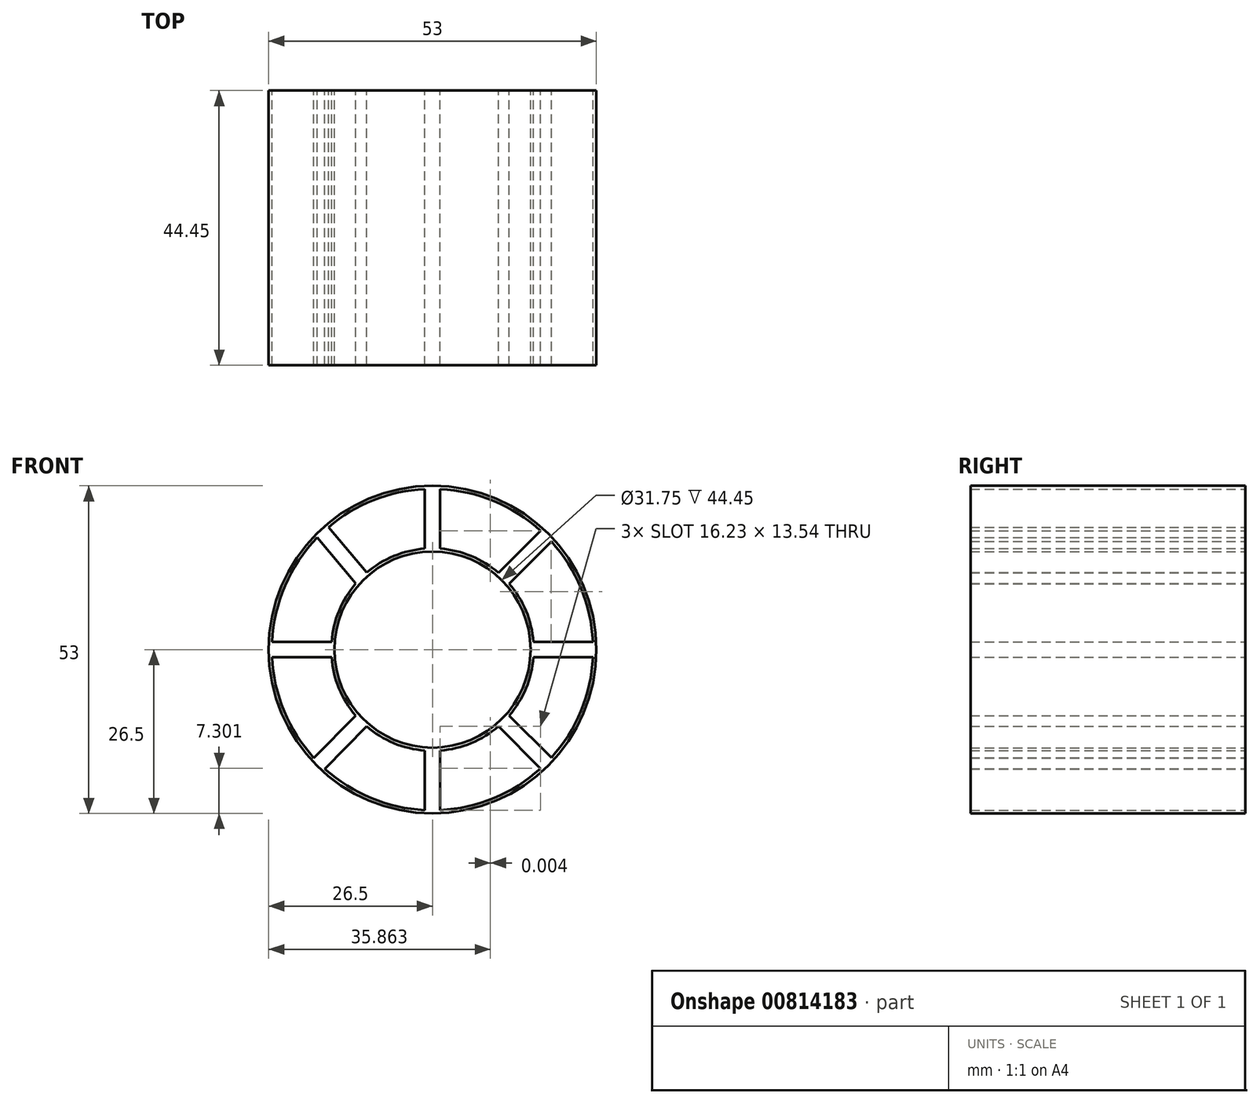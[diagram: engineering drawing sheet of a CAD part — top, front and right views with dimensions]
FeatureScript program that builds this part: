
annotation { "Feature Type Name" : "Feature", "Feature Type Description" : "" }
export const myFeature = defineFeature(function(context is Context, id is Id, definition is map)
    precondition{}
    {
        {
            var Q0;
            Q0=qCreatedBy(makeId("Front.planeOp"),FACE);
            var sketch = newSketch(context, id + "F0", { "sketchPlane" : qUnion([Q0])});
            skCircle(sketch, "E0", {"center": v(0, 0) * mm, "radius": 26.5 * mm});
            skCircle(sketch, "E1", {"center": v(0, 0) * mm, "radius": 15.88 * mm});
            skPoint(sketch, "E2", {"position": v(0, 15.88) * mm});
            skPoint(sketch, "E3", {"position": v(-11.23, 11.23) * mm});
            skPoint(sketch, "E4", {"position": v(-15.88, 0) * mm});
            skPoint(sketch, "E5", {"position": v(-11.23, -11.23) * mm});
            skPoint(sketch, "E6", {"position": v(0, -15.88) * mm});
            skPoint(sketch, "E7", {"position": v(11.23, -11.23) * mm});
            skPoint(sketch, "E8", {"position": v(15.88, 0) * mm});
            skPoint(sketch, "E9", {"position": v(11.23, 11.23) * mm});
            skPoint(sketch, "E10", {"position": v(-1.25, 15.83) * mm});
            skPoint(sketch, "E11", {"position": v(1.25, 15.83) * mm});
            skPoint(sketch, "E12", {"position": v(10.3, 12.07) * mm});
            skPoint(sketch, "E13", {"position": v(12.07, 10.3) * mm});
            skPoint(sketch, "E14", {"position": v(15.83, 1.25) * mm});
            skPoint(sketch, "E15", {"position": v(15.83, -1.25) * mm});
            skPoint(sketch, "E16", {"position": v(10.3, -12.07) * mm});
            skPoint(sketch, "E17", {"position": v(12.07, -10.3) * mm});
            skPoint(sketch, "E18", {"position": v(1.25, -15.83) * mm});
            skPoint(sketch, "E19", {"position": v(-1.25, -15.83) * mm});
            skPoint(sketch, "E20", {"position": v(-10.3, -12.07) * mm});
            skPoint(sketch, "E21", {"position": v(-12.07, -10.3) * mm});
            skPoint(sketch, "E22", {"position": v(-15.83, -1.25) * mm});
            skPoint(sketch, "E23", {"position": v(-15.83, 1.25) * mm});
            skPoint(sketch, "E24", {"position": v(-12.07, 10.3) * mm});
            skPoint(sketch, "E25", {"position": v(-10.3, 12.07) * mm});
            skLineSegment(sketch, "E26", {"start": v(-1.25, 15.83) * mm, "end": v(-1.25, 26.47) * mm});
            skLineSegment(sketch, "E27", {"start": v(1.25, 15.83) * mm, "end": v(1.25, 26.47) * mm});
            skLineSegment(sketch, "E28", {"start": v(10.3, 12.07) * mm, "end": v(17.84, 19.6) * mm});
            skLineSegment(sketch, "E29", {"start": v(12.07, 10.3) * mm, "end": v(19.6, 17.83) * mm});
            skLineSegment(sketch, "E30", {"start": v(15.83, 1.25) * mm, "end": v(26.47, 1.25) * mm});
            skLineSegment(sketch, "E31", {"start": v(15.83, -1.25) * mm, "end": v(26.47, -1.25) * mm});
            skLineSegment(sketch, "E32", {"start": v(12.07, -10.3) * mm, "end": v(19.6, -17.84) * mm});
            skLineSegment(sketch, "E33", {"start": v(10.3, -12.07) * mm, "end": v(17.83, -19.6) * mm});
            skLineSegment(sketch, "E34", {"start": v(-1.25, -15.83) * mm, "end": v(-1.25, -26.47) * mm});
            skLineSegment(sketch, "E35", {"start": v(1.25, -15.83) * mm, "end": v(1.25, -26.47) * mm});
            skLineSegment(sketch, "E36", {"start": v(-12.07, -10.3) * mm, "end": v(-19.54, -17.9) * mm});
            skLineSegment(sketch, "E37", {"start": v(-10.3, -12.07) * mm, "end": v(-17.77, -19.66) * mm});
            skLineSegment(sketch, "E38", {"start": v(-15.83, 1.25) * mm, "end": v(-26.47, 1.25) * mm});
            skLineSegment(sketch, "E39", {"start": v(-15.83, -1.25) * mm, "end": v(-26.47, -1.25) * mm});
            skLineSegment(sketch, "E40", {"start": v(-12.07, 10.3) * mm, "end": v(-18.98, 18.5) * mm});
            skLineSegment(sketch, "E41", {"start": v(-10.3, 12.07) * mm, "end": v(-17.16, 20.2) * mm});
            skCircle(sketch, "E42", {"center": v(0, 0) * mm, "radius": 26 * mm});
            skCircle(sketch, "E43", {"center": v(0, 0) * mm, "radius": 16.38 * mm});
            skSolve(sketch);
        }
        {
            var Q0;
            {var subQ0=sQuery(id+"F0.wireOp",EDGE,"E26");var subQ1=sQuery(id+"F0.wireOp",EDGE,"E1");var subQ2=makeQuery(id+"F0.imprint","INTERSECT",VERTEX,{"derivedFrom":[subQ1,subQ0]});Q0=makeQuery(id+"F0.imprint","IMPRINT",FACE,{"disambiguationData":[TD([[makeQuery(id+"F0.imprint","IMPRINT",EDGE,{"disambiguationData":[TD([[subQ2,-1.0]])],"derivedFrom":subQ1}),-1.0]])]});}
            var Q1;
            {var subQ0=sQuery(id+"F0.wireOp",EDGE,"E26");var subQ1=sQuery(id+"F0.wireOp",EDGE,"E1");var subQ2=makeQuery(id+"F0.imprint","INTERSECT",VERTEX,{"derivedFrom":[subQ1,subQ0]});Q1=makeQuery(id+"F0.imprint","IMPRINT",FACE,{"disambiguationData":[TD([[makeQuery(id+"F0.imprint","IMPRINT",EDGE,{"disambiguationData":[TD([[subQ2,1.0]])],"derivedFrom":subQ1}),-1.0]])]});}
            var Q2;
            {var subQ0=sQuery(id+"F0.wireOp",EDGE,"E40");var subQ1=sQuery(id+"F0.wireOp",EDGE,"E1");var subQ2=makeQuery(id+"F0.imprint","INTERSECT",VERTEX,{"derivedFrom":[subQ1,subQ0]});Q2=makeQuery(id+"F0.imprint","IMPRINT",FACE,{"disambiguationData":[TD([[makeQuery(id+"F0.imprint","IMPRINT",EDGE,{"disambiguationData":[TD([[subQ2,1.0]])],"derivedFrom":subQ1}),-1.0]])]});}
            var Q3;
            {var subQ0=sQuery(id+"F0.wireOp",EDGE,"E38");var subQ1=sQuery(id+"F0.wireOp",EDGE,"E1");var subQ2=makeQuery(id+"F0.imprint","INTERSECT",VERTEX,{"derivedFrom":[subQ1,subQ0]});Q3=makeQuery(id+"F0.imprint","IMPRINT",FACE,{"disambiguationData":[TD([[makeQuery(id+"F0.imprint","IMPRINT",EDGE,{"disambiguationData":[TD([[subQ2,1.0]])],"derivedFrom":subQ1}),-1.0]])]});}
            var Q4;
            {var subQ0=sQuery(id+"F0.wireOp",EDGE,"E38");var subQ1=sQuery(id+"F0.wireOp",EDGE,"E1");var subQ2=makeQuery(id+"F0.imprint","INTERSECT",VERTEX,{"derivedFrom":[subQ1,subQ0]});Q4=makeQuery(id+"F0.imprint","IMPRINT",FACE,{"disambiguationData":[TD([[makeQuery(id+"F0.imprint","IMPRINT",EDGE,{"disambiguationData":[TD([[subQ2,-1.0]])],"derivedFrom":subQ1}),-1.0]])]});}
            var Q5;
            {var subQ0=sQuery(id+"F0.wireOp",EDGE,"E36");var subQ1=sQuery(id+"F0.wireOp",EDGE,"E1");var subQ2=makeQuery(id+"F0.imprint","INTERSECT",VERTEX,{"derivedFrom":[subQ1,subQ0]});Q5=makeQuery(id+"F0.imprint","IMPRINT",FACE,{"disambiguationData":[TD([[makeQuery(id+"F0.imprint","IMPRINT",EDGE,{"disambiguationData":[TD([[subQ2,1.0]])],"derivedFrom":subQ1}),-1.0]])]});}
            var Q6;
            {var subQ0=sQuery(id+"F0.wireOp",EDGE,"E27");var subQ1=sQuery(id+"F0.wireOp",EDGE,"E1");var subQ2=makeQuery(id+"F0.imprint","INTERSECT",VERTEX,{"derivedFrom":[subQ1,subQ0]});Q6=makeQuery(id+"F0.imprint","IMPRINT",FACE,{"disambiguationData":[TD([[makeQuery(id+"F0.imprint","IMPRINT",EDGE,{"disambiguationData":[TD([[subQ2,1.0]])],"derivedFrom":subQ1}),-1.0]])]});}
            var Q7;
            {var subQ0=sQuery(id+"F0.wireOp",EDGE,"E28");var subQ1=sQuery(id+"F0.wireOp",EDGE,"E1");var subQ2=makeQuery(id+"F0.imprint","INTERSECT",VERTEX,{"derivedFrom":[subQ1,subQ0]});Q7=makeQuery(id+"F0.imprint","IMPRINT",FACE,{"disambiguationData":[TD([[makeQuery(id+"F0.imprint","IMPRINT",EDGE,{"disambiguationData":[TD([[subQ2,1.0]])],"derivedFrom":subQ1}),-1.0]])]});}
            var Q8;
            {var subQ0=sQuery(id+"F0.wireOp",EDGE,"E29");var subQ1=sQuery(id+"F0.wireOp",EDGE,"E1");var subQ2=makeQuery(id+"F0.imprint","INTERSECT",VERTEX,{"derivedFrom":[subQ1,subQ0]});Q8=makeQuery(id+"F0.imprint","IMPRINT",FACE,{"disambiguationData":[TD([[makeQuery(id+"F0.imprint","IMPRINT",EDGE,{"disambiguationData":[TD([[subQ2,1.0]])],"derivedFrom":subQ1}),-1.0]])]});}
            var Q9;
            {var subQ0=sQuery(id+"F0.wireOp",EDGE,"E30");var subQ1=sQuery(id+"F0.wireOp",EDGE,"E1");var subQ2=makeQuery(id+"F0.imprint","INTERSECT",VERTEX,{"derivedFrom":[subQ1,subQ0]});Q9=makeQuery(id+"F0.imprint","IMPRINT",FACE,{"disambiguationData":[TD([[makeQuery(id+"F0.imprint","IMPRINT",EDGE,{"disambiguationData":[TD([[subQ2,1.0]])],"derivedFrom":subQ1}),-1.0]])]});}
            var Q10;
            {var subQ0=sQuery(id+"F0.wireOp",EDGE,"E31");var subQ1=sQuery(id+"F0.wireOp",EDGE,"E1");var subQ2=makeQuery(id+"F0.imprint","INTERSECT",VERTEX,{"derivedFrom":[subQ1,subQ0]});Q10=makeQuery(id+"F0.imprint","IMPRINT",FACE,{"disambiguationData":[TD([[makeQuery(id+"F0.imprint","IMPRINT",EDGE,{"disambiguationData":[TD([[subQ2,1.0]])],"derivedFrom":subQ1}),-1.0]])]});}
            var Q11;
            {var subQ0=sQuery(id+"F0.wireOp",EDGE,"E32");var subQ1=sQuery(id+"F0.wireOp",EDGE,"E1");var subQ2=makeQuery(id+"F0.imprint","INTERSECT",VERTEX,{"derivedFrom":[subQ1,subQ0]});Q11=makeQuery(id+"F0.imprint","IMPRINT",FACE,{"disambiguationData":[TD([[makeQuery(id+"F0.imprint","IMPRINT",EDGE,{"disambiguationData":[TD([[subQ2,1.0]])],"derivedFrom":subQ1}),-1.0]])]});}
            var Q12;
            {var subQ0=sQuery(id+"F0.wireOp",EDGE,"E33");var subQ1=sQuery(id+"F0.wireOp",EDGE,"E1");var subQ2=makeQuery(id+"F0.imprint","INTERSECT",VERTEX,{"derivedFrom":[subQ1,subQ0]});Q12=makeQuery(id+"F0.imprint","IMPRINT",FACE,{"disambiguationData":[TD([[makeQuery(id+"F0.imprint","IMPRINT",EDGE,{"disambiguationData":[TD([[subQ2,1.0]])],"derivedFrom":subQ1}),-1.0]])]});}
            var Q13;
            {var subQ0=sQuery(id+"F0.wireOp",EDGE,"E34");var subQ1=sQuery(id+"F0.wireOp",EDGE,"E1");var subQ2=makeQuery(id+"F0.imprint","INTERSECT",VERTEX,{"derivedFrom":[subQ1,subQ0]});Q13=makeQuery(id+"F0.imprint","IMPRINT",FACE,{"disambiguationData":[TD([[makeQuery(id+"F0.imprint","IMPRINT",EDGE,{"disambiguationData":[TD([[subQ2,-1.0]])],"derivedFrom":subQ1}),-1.0]])]});}
            var Q14;
            {var subQ0=sQuery(id+"F0.wireOp",EDGE,"E34");var subQ1=sQuery(id+"F0.wireOp",EDGE,"E1");var subQ2=makeQuery(id+"F0.imprint","INTERSECT",VERTEX,{"derivedFrom":[subQ1,subQ0]});Q14=makeQuery(id+"F0.imprint","IMPRINT",FACE,{"disambiguationData":[TD([[makeQuery(id+"F0.imprint","IMPRINT",EDGE,{"disambiguationData":[TD([[subQ2,1.0]])],"derivedFrom":subQ1}),-1.0]])]});}
            var Q15;
            {var subQ0=sQuery(id+"F0.wireOp",EDGE,"E36");var subQ1=sQuery(id+"F0.wireOp",EDGE,"E1");var subQ2=makeQuery(id+"F0.imprint","INTERSECT",VERTEX,{"derivedFrom":[subQ1,subQ0]});Q15=makeQuery(id+"F0.imprint","IMPRINT",FACE,{"disambiguationData":[TD([[makeQuery(id+"F0.imprint","IMPRINT",EDGE,{"disambiguationData":[TD([[subQ2,-1.0]])],"derivedFrom":subQ1}),-1.0]])]});}
            var Q16;
            {var subQ0=sQuery(id+"F0.wireOp",EDGE,"E43");var subQ1=sQuery(id+"F0.wireOp",EDGE,"E38");var subQ2=makeQuery(id+"F0.imprint","INTERSECT",VERTEX,{"derivedFrom":[subQ1,subQ0]});Q16=makeQuery(id+"F0.imprint","IMPRINT",FACE,{"disambiguationData":[TD([[makeQuery(id+"F0.imprint","IMPRINT",EDGE,{"disambiguationData":[TD([[subQ2,-1.0]])],"derivedFrom":subQ1}),1.0]])]});}
            var Q17;
            {var subQ0=sQuery(id+"F0.wireOp",EDGE,"E43");var subQ1=sQuery(id+"F0.wireOp",EDGE,"E40");var subQ2=makeQuery(id+"F0.imprint","INTERSECT",VERTEX,{"derivedFrom":[subQ1,subQ0]});Q17=makeQuery(id+"F0.imprint","IMPRINT",FACE,{"disambiguationData":[TD([[makeQuery(id+"F0.imprint","IMPRINT",EDGE,{"disambiguationData":[TD([[subQ2,-1.0]])],"derivedFrom":subQ1}),-1.0]])]});}
            var Q18;
            {var subQ0=sQuery(id+"F0.wireOp",EDGE,"E43");var subQ1=sQuery(id+"F0.wireOp",EDGE,"E26");var subQ2=makeQuery(id+"F0.imprint","INTERSECT",VERTEX,{"derivedFrom":[subQ1,subQ0]});Q18=makeQuery(id+"F0.imprint","IMPRINT",FACE,{"disambiguationData":[TD([[makeQuery(id+"F0.imprint","IMPRINT",EDGE,{"disambiguationData":[TD([[subQ2,-1.0]])],"derivedFrom":subQ1}),-1.0]])]});}
            var Q19;
            {var subQ0=sQuery(id+"F0.wireOp",EDGE,"E43");var subQ1=sQuery(id+"F0.wireOp",EDGE,"E28");var subQ2=makeQuery(id+"F0.imprint","INTERSECT",VERTEX,{"derivedFrom":[subQ1,subQ0]});Q19=makeQuery(id+"F0.imprint","IMPRINT",FACE,{"disambiguationData":[TD([[makeQuery(id+"F0.imprint","IMPRINT",EDGE,{"disambiguationData":[TD([[subQ2,-1.0]])],"derivedFrom":subQ1}),-1.0]])]});}
            var Q20;
            {var subQ0=sQuery(id+"F0.wireOp",EDGE,"E43");var subQ1=sQuery(id+"F0.wireOp",EDGE,"E30");var subQ2=makeQuery(id+"F0.imprint","INTERSECT",VERTEX,{"derivedFrom":[subQ1,subQ0]});Q20=makeQuery(id+"F0.imprint","IMPRINT",FACE,{"disambiguationData":[TD([[makeQuery(id+"F0.imprint","IMPRINT",EDGE,{"disambiguationData":[TD([[subQ2,-1.0]])],"derivedFrom":subQ1}),-1.0]])]});}
            var Q21;
            {var subQ0=sQuery(id+"F0.wireOp",EDGE,"E43");var subQ1=sQuery(id+"F0.wireOp",EDGE,"E32");var subQ2=makeQuery(id+"F0.imprint","INTERSECT",VERTEX,{"derivedFrom":[subQ1,subQ0]});Q21=makeQuery(id+"F0.imprint","IMPRINT",FACE,{"disambiguationData":[TD([[makeQuery(id+"F0.imprint","IMPRINT",EDGE,{"disambiguationData":[TD([[subQ2,-1.0]])],"derivedFrom":subQ1}),-1.0]])]});}
            var Q22;
            {var subQ0=sQuery(id+"F0.wireOp",EDGE,"E43");var subQ1=sQuery(id+"F0.wireOp",EDGE,"E34");var subQ2=makeQuery(id+"F0.imprint","INTERSECT",VERTEX,{"derivedFrom":[subQ1,subQ0]});Q22=makeQuery(id+"F0.imprint","IMPRINT",FACE,{"disambiguationData":[TD([[makeQuery(id+"F0.imprint","IMPRINT",EDGE,{"disambiguationData":[TD([[subQ2,-1.0]])],"derivedFrom":subQ1}),1.0]])]});}
            var Q23;
            {var subQ0=sQuery(id+"F0.wireOp",EDGE,"E43");var subQ1=sQuery(id+"F0.wireOp",EDGE,"E36");var subQ2=makeQuery(id+"F0.imprint","INTERSECT",VERTEX,{"derivedFrom":[subQ1,subQ0]});Q23=makeQuery(id+"F0.imprint","IMPRINT",FACE,{"disambiguationData":[TD([[makeQuery(id+"F0.imprint","IMPRINT",EDGE,{"disambiguationData":[TD([[subQ2,-1.0]])],"derivedFrom":subQ1}),1.0]])]});}
            var Q24;
            {var subQ0=sQuery(id+"F0.wireOp",EDGE,"E36");var subQ1=sQuery(id+"F0.wireOp",EDGE,"E0");var subQ2=makeQuery(id+"F0.imprint","INTERSECT",VERTEX,{"derivedFrom":[subQ1,subQ0]});Q24=makeQuery(id+"F0.imprint","IMPRINT",FACE,{"disambiguationData":[TD([[makeQuery(id+"F0.imprint","IMPRINT",EDGE,{"disambiguationData":[TD([[subQ2,1.0]])],"derivedFrom":subQ1}),1.0]])]});}
            var Q25;
            {var subQ0=sQuery(id+"F0.wireOp",EDGE,"E38");var subQ1=sQuery(id+"F0.wireOp",EDGE,"E0");var subQ2=makeQuery(id+"F0.imprint","INTERSECT",VERTEX,{"derivedFrom":[subQ1,subQ0]});Q25=makeQuery(id+"F0.imprint","IMPRINT",FACE,{"disambiguationData":[TD([[makeQuery(id+"F0.imprint","IMPRINT",EDGE,{"disambiguationData":[TD([[subQ2,-1.0]])],"derivedFrom":subQ1}),1.0]])]});}
            var Q26;
            {var subQ0=sQuery(id+"F0.wireOp",EDGE,"E38");var subQ1=sQuery(id+"F0.wireOp",EDGE,"E0");var subQ2=makeQuery(id+"F0.imprint","INTERSECT",VERTEX,{"derivedFrom":[subQ1,subQ0]});Q26=makeQuery(id+"F0.imprint","IMPRINT",FACE,{"disambiguationData":[TD([[makeQuery(id+"F0.imprint","IMPRINT",EDGE,{"disambiguationData":[TD([[subQ2,1.0]])],"derivedFrom":subQ1}),1.0]])]});}
            var Q27;
            {var subQ0=sQuery(id+"F0.wireOp",EDGE,"E40");var subQ1=sQuery(id+"F0.wireOp",EDGE,"E0");var subQ2=makeQuery(id+"F0.imprint","INTERSECT",VERTEX,{"derivedFrom":[subQ1,subQ0]});Q27=makeQuery(id+"F0.imprint","IMPRINT",FACE,{"disambiguationData":[TD([[makeQuery(id+"F0.imprint","IMPRINT",EDGE,{"disambiguationData":[TD([[subQ2,1.0]])],"derivedFrom":subQ1}),1.0]])]});}
            var Q28;
            {var subQ0=sQuery(id+"F0.wireOp",EDGE,"E26");var subQ1=sQuery(id+"F0.wireOp",EDGE,"E0");var subQ2=makeQuery(id+"F0.imprint","INTERSECT",VERTEX,{"derivedFrom":[subQ1,subQ0]});Q28=makeQuery(id+"F0.imprint","IMPRINT",FACE,{"disambiguationData":[TD([[makeQuery(id+"F0.imprint","IMPRINT",EDGE,{"disambiguationData":[TD([[subQ2,-1.0]])],"derivedFrom":subQ1}),1.0]])]});}
            var Q29;
            {var subQ0=sQuery(id+"F0.wireOp",EDGE,"E26");var subQ1=sQuery(id+"F0.wireOp",EDGE,"E0");var subQ2=makeQuery(id+"F0.imprint","INTERSECT",VERTEX,{"derivedFrom":[subQ1,subQ0]});Q29=makeQuery(id+"F0.imprint","IMPRINT",FACE,{"disambiguationData":[TD([[makeQuery(id+"F0.imprint","IMPRINT",EDGE,{"disambiguationData":[TD([[subQ2,1.0]])],"derivedFrom":subQ1}),1.0]])]});}
            var Q30;
            {var subQ0=sQuery(id+"F0.wireOp",EDGE,"E27");var subQ1=sQuery(id+"F0.wireOp",EDGE,"E0");var subQ2=makeQuery(id+"F0.imprint","INTERSECT",VERTEX,{"derivedFrom":[subQ1,subQ0]});Q30=makeQuery(id+"F0.imprint","IMPRINT",FACE,{"disambiguationData":[TD([[makeQuery(id+"F0.imprint","IMPRINT",EDGE,{"disambiguationData":[TD([[subQ2,1.0]])],"derivedFrom":subQ1}),1.0]])]});}
            var Q31;
            {var subQ0=sQuery(id+"F0.wireOp",EDGE,"E28");var subQ1=sQuery(id+"F0.wireOp",EDGE,"E0");var subQ2=makeQuery(id+"F0.imprint","INTERSECT",VERTEX,{"derivedFrom":[subQ1,subQ0]});Q31=makeQuery(id+"F0.imprint","IMPRINT",FACE,{"disambiguationData":[TD([[makeQuery(id+"F0.imprint","IMPRINT",EDGE,{"disambiguationData":[TD([[subQ2,1.0]])],"derivedFrom":subQ1}),1.0]])]});}
            var Q32;
            {var subQ0=sQuery(id+"F0.wireOp",EDGE,"E29");var subQ1=sQuery(id+"F0.wireOp",EDGE,"E0");var subQ2=makeQuery(id+"F0.imprint","INTERSECT",VERTEX,{"derivedFrom":[subQ1,subQ0]});Q32=makeQuery(id+"F0.imprint","IMPRINT",FACE,{"disambiguationData":[TD([[makeQuery(id+"F0.imprint","IMPRINT",EDGE,{"disambiguationData":[TD([[subQ2,1.0]])],"derivedFrom":subQ1}),1.0]])]});}
            var Q33;
            {var subQ0=sQuery(id+"F0.wireOp",EDGE,"E30");var subQ1=sQuery(id+"F0.wireOp",EDGE,"E0");var subQ2=makeQuery(id+"F0.imprint","INTERSECT",VERTEX,{"derivedFrom":[subQ1,subQ0]});Q33=makeQuery(id+"F0.imprint","IMPRINT",FACE,{"disambiguationData":[TD([[makeQuery(id+"F0.imprint","IMPRINT",EDGE,{"disambiguationData":[TD([[subQ2,1.0]])],"derivedFrom":subQ1}),1.0]])]});}
            var Q34;
            {var subQ0=sQuery(id+"F0.wireOp",EDGE,"E31");var subQ1=sQuery(id+"F0.wireOp",EDGE,"E0");var subQ2=makeQuery(id+"F0.imprint","INTERSECT",VERTEX,{"derivedFrom":[subQ1,subQ0]});Q34=makeQuery(id+"F0.imprint","IMPRINT",FACE,{"disambiguationData":[TD([[makeQuery(id+"F0.imprint","IMPRINT",EDGE,{"disambiguationData":[TD([[subQ2,1.0]])],"derivedFrom":subQ1}),1.0]])]});}
            var Q35;
            {var subQ0=sQuery(id+"F0.wireOp",EDGE,"E32");var subQ1=sQuery(id+"F0.wireOp",EDGE,"E0");var subQ2=makeQuery(id+"F0.imprint","INTERSECT",VERTEX,{"derivedFrom":[subQ1,subQ0]});Q35=makeQuery(id+"F0.imprint","IMPRINT",FACE,{"disambiguationData":[TD([[makeQuery(id+"F0.imprint","IMPRINT",EDGE,{"disambiguationData":[TD([[subQ2,1.0]])],"derivedFrom":subQ1}),1.0]])]});}
            var Q36;
            {var subQ0=sQuery(id+"F0.wireOp",EDGE,"E33");var subQ1=sQuery(id+"F0.wireOp",EDGE,"E0");var subQ2=makeQuery(id+"F0.imprint","INTERSECT",VERTEX,{"derivedFrom":[subQ1,subQ0]});Q36=makeQuery(id+"F0.imprint","IMPRINT",FACE,{"disambiguationData":[TD([[makeQuery(id+"F0.imprint","IMPRINT",EDGE,{"disambiguationData":[TD([[subQ2,1.0]])],"derivedFrom":subQ1}),1.0]])]});}
            var Q37;
            {var subQ0=sQuery(id+"F0.wireOp",EDGE,"E34");var subQ1=sQuery(id+"F0.wireOp",EDGE,"E0");var subQ2=makeQuery(id+"F0.imprint","INTERSECT",VERTEX,{"derivedFrom":[subQ1,subQ0]});Q37=makeQuery(id+"F0.imprint","IMPRINT",FACE,{"disambiguationData":[TD([[makeQuery(id+"F0.imprint","IMPRINT",EDGE,{"disambiguationData":[TD([[subQ2,-1.0]])],"derivedFrom":subQ1}),1.0]])]});}
            var Q38;
            {var subQ0=sQuery(id+"F0.wireOp",EDGE,"E34");var subQ1=sQuery(id+"F0.wireOp",EDGE,"E0");var subQ2=makeQuery(id+"F0.imprint","INTERSECT",VERTEX,{"derivedFrom":[subQ1,subQ0]});Q38=makeQuery(id+"F0.imprint","IMPRINT",FACE,{"disambiguationData":[TD([[makeQuery(id+"F0.imprint","IMPRINT",EDGE,{"disambiguationData":[TD([[subQ2,1.0]])],"derivedFrom":subQ1}),1.0]])]});}
            var Q39;
            {var subQ0=sQuery(id+"F0.wireOp",EDGE,"E36");var subQ1=sQuery(id+"F0.wireOp",EDGE,"E0");var subQ2=makeQuery(id+"F0.imprint","INTERSECT",VERTEX,{"derivedFrom":[subQ1,subQ0]});Q39=makeQuery(id+"F0.imprint","IMPRINT",FACE,{"disambiguationData":[TD([[makeQuery(id+"F0.imprint","IMPRINT",EDGE,{"disambiguationData":[TD([[subQ2,-1.0]])],"derivedFrom":subQ1}),1.0]])]});}
            extrude(context, id + "F1", {"entities" : qUnion([Q0, Q1, Q2, Q3, Q4, Q5, Q6, Q7, Q8, Q9, Q10, Q11, Q12, Q13, Q14, Q15, Q16, Q17, Q18, Q19, Q20, Q21, Q22, Q23, Q24, Q25, Q26, Q27, Q28, Q29, Q30, Q31, Q32, Q33, Q34, Q35, Q36, Q37, Q38, Q39]), "depth" : 44.45 * mm, "offsetDistance" : 25 * mm});
        }
    });
